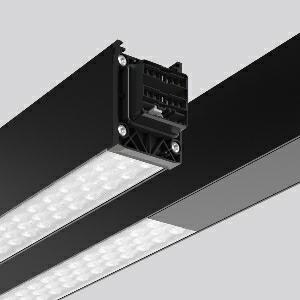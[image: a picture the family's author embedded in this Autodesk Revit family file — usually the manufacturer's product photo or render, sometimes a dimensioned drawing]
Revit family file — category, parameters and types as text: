
# Revit family: linedo_2_3m_30_1100_952330_833_500_503_2cd3
name_source: partatom
category: Lighting Fixtures
units: mm (PartAtom-declared; Revit-internal decimal feet)

## family parameters
Cut with Voids When Loaded = No
Host = Face
Light Source = No
Part Type = Normal
Room Calculation Point = No
Round Connector Dimension = Use Diameter
Shared = No

## types (1)
- LINEDO_2,3m_30_1100 (1 x LED Modul 830, 3900 lm, 3000)
    Apparent Load = 55 VA
    CIE Flux Codes = 89 97 99 100 100
    Color Rendering = 80
    Color Temperature = 3000
    Default Elevation = 1800 mm
    Description = LINEDO, 55 W, 7800 lm, 830, black, on/off
Continuous line luminaire, L 2291 B 58 H 76
    Height = 76 mm
    Lamp = 1 x LED Modul 830
    Lamp Light Flux = 3900 lm
    Lamp count = 1
    Length = 2291 mm
    Lifetime = 50000 h
    Luminous efficacy = 142 lm/W
    Manufacturer = RZB
    ModVariant = No
    Model = 952330.833.500.503
    Mounting Place = Ceiling
    Mounting Type = Surface mounted, Pendant
    Number of Poles = 1
    OnlyDefault = Yes
    Power Factor = 1
    Product Name = LINEDO_2,3m_30_1100
    Product group = Continuous line luminaire system Linedo IP 54
    ProductGroupID = 314
    Protection Class = Protection class I
    Protection Degree = IP 54
    RLX_Detail_Level = 1
    RLX_Emergency_Light_Flux = 0 lm
    RLX_Emergency_Type = 0
    RLX_Emergency_Type_DB = No
    RlxData = <blob elided: 56597 chars, md5=addfbc14>
    Socket = socket
    Standby Power = 0 W
    System Light Flux = 7800 lm
    System Power = 55 W
    Type Comments = Product without accessories
    Type Image = 954530.853.476.504.jpg
    URL = http://relux.com
    VarID = ---
    Voltage = 230 V
    Voltage Range = 220-240 V
    Weight = 0.00 kg
    Width = 58 mm

## geometry (parser evidence)
native form markers: Blend x4, Sweep x18
no freeform markers — native parametric forms only
